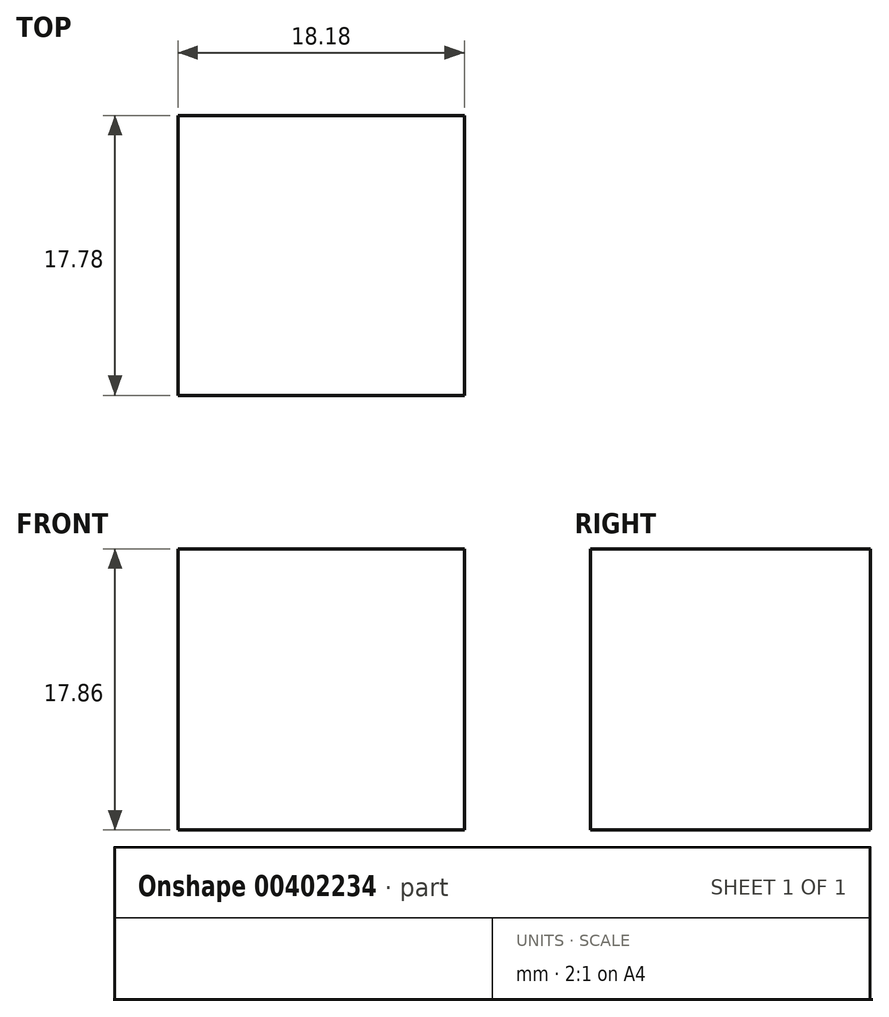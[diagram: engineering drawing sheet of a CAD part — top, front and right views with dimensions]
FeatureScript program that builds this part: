
annotation { "Feature Type Name" : "Feature", "Feature Type Description" : "" }
export const myFeature = defineFeature(function(context is Context, id is Id, definition is map)
    precondition{}
    {
        {
            var Q0;
            Q0=qCreatedBy(makeId("Front.planeOp"),FACE);
            var sketch = newSketch(context, id + "F0", { "sketchPlane" : qUnion([Q0])});
            skLineSegment(sketch, "E0.bottom", {"start": v(0, 0) * mm, "end": v(18.18, 0) * mm});
            skLineSegment(sketch, "E0.top", {"start": v(0, 17.86) * mm, "end": v(18.18, 17.86) * mm});
            skLineSegment(sketch, "E0.left", {"start": v(0, 0) * mm, "end": v(0, 17.86) * mm});
            skLineSegment(sketch, "E0.right", {"start": v(18.18, 0) * mm, "end": v(18.18, 17.86) * mm});
            skSolve(sketch);
        }
        {
            var Q0;
            Q0=makeQuery(id+"F0.imprint","IMPRINT",FACE,{"disambiguationData":[TD([[makeQuery(id+"F0.imprint","IMPRINT",EDGE,{"derivedFrom":sQuery(id+"F0.wireOp",EDGE,"E0.bottom")}),1.0]])]});
            extrude(context, id + "F1", {"entities" : qUnion([Q0]), "depth" : 17.78 * mm});
        }
    });
